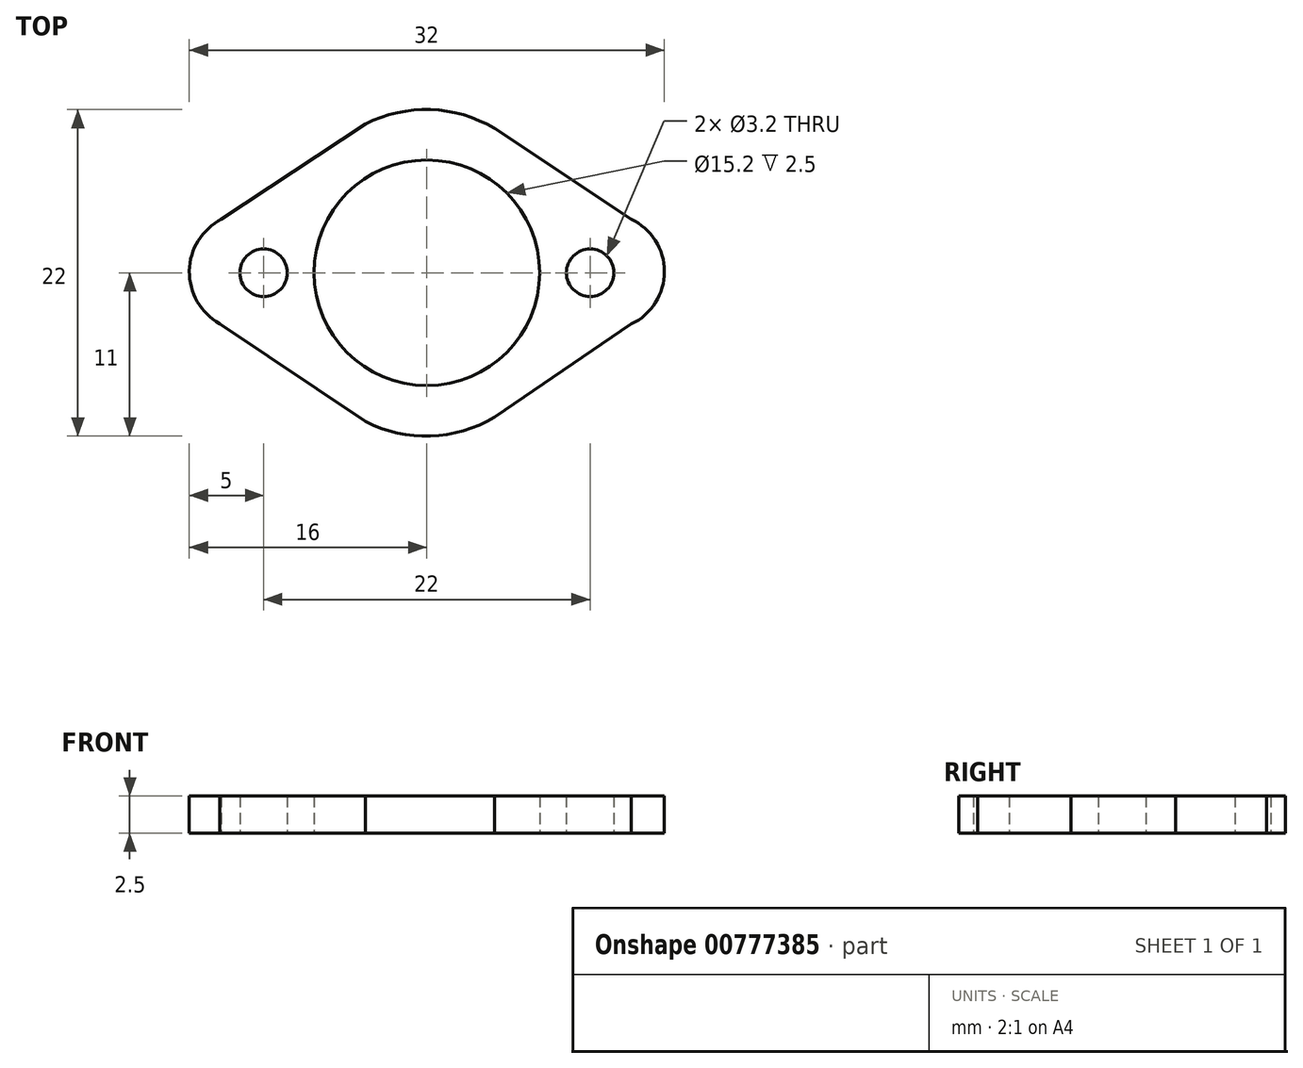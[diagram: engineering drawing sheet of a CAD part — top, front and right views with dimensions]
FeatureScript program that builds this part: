
annotation { "Feature Type Name" : "Feature", "Feature Type Description" : "" }
export const myFeature = defineFeature(function(context is Context, id is Id, definition is map)
    precondition{}
    {
        {
            var Q0;
            Q0=qCreatedBy(makeId("Top.planeOp"),FACE);
            var sketch = newSketch(context, id + "F0", { "sketchPlane" : qUnion([Q0])});
            skCircle(sketch, "E0", {"center": v(0, 0) * mm, "radius": 7.6 * mm});
            skCircle(sketch, "E1", {"center": v(11, 0) * mm, "radius": 1.6 * mm});
            skCircle(sketch, "E2", {"center": v(-11, 0) * mm, "radius": 1.6 * mm});
            skLineSegment(sketch, "E3", {"start": v(-13.34, 2.74) * mm, "end": v(-3.64, 9.15) * mm});
            skLineSegment(sketch, "E4", {"start": v(4.01, 8.89) * mm, "end": v(13.28, 2.74) * mm});
            skLineSegment(sketch, "E5", {"start": v(13.28, -2.58) * mm, "end": v(4.02, -8.88) * mm});
            skLineSegment(sketch, "E6", {"start": v(-3.64, -9.16) * mm, "end": v(-13.43, -2.58) * mm});
            skPoint(sketch, "E7.visualSharp", {"position": v(-21.18, 0) * mm});
            skArc(sketch, "E7.filletArc", {"start": v(-13.34, 2.74) * mm, "mid": v(-15, 0.1) * mm, "end": v(-13.43, -2.58) * mm});
            skPoint(sketch, "E8.visualSharp", {"position": v(0, 10.6) * mm});
            skArc(sketch, "E8.filletArc", {"start": v(4.01, 8.89) * mm, "mid": v(0.22, 10) * mm, "end": v(-3.64, 9.15) * mm});
            skPoint(sketch, "E9.visualSharp", {"position": v(17.4, 0) * mm});
            skArc(sketch, "E9.filletArc", {"start": v(13.28, -2.58) * mm, "mid": v(15, 0.08) * mm, "end": v(13.28, 2.74) * mm});
            skPoint(sketch, "E10.visualSharp", {"position": v(0, -10.6) * mm});
            skArc(sketch, "E10.filletArc", {"start": v(-3.64, -9.16) * mm, "mid": v(0.23, -10) * mm, "end": v(4.02, -8.88) * mm});
            skLineSegment(sketch, "E11.0", {"start": v(4.54, 9.73) * mm, "end": v(13.77, 3.61) * mm});
            skArc(sketch, "E11.1", {"start": v(13.77, -3.45) * mm, "mid": v(16, 0.08) * mm, "end": v(13.77, 3.61) * mm});
            skArc(sketch, "E11.2", {"start": v(4.54, 9.73) * mm, "mid": v(0.24, 11) * mm, "end": v(-4.14, 10.02) * mm});
            skLineSegment(sketch, "E11.3", {"start": v(13.77, -3.45) * mm, "end": v(4.56, -9.73) * mm});
            skLineSegment(sketch, "E11.4", {"start": v(-13.84, 3.6) * mm, "end": v(-4.14, 10.02) * mm});
            skArc(sketch, "E11.5", {"start": v(-13.84, 3.6) * mm, "mid": v(-16, 0.12) * mm, "end": v(-13.95, -3.44) * mm});
            skLineSegment(sketch, "E11.6", {"start": v(-4.14, -10.02) * mm, "end": v(-13.95, -3.44) * mm});
            skArc(sketch, "E11.7", {"start": v(-4.14, -10.02) * mm, "mid": v(0.25, -11) * mm, "end": v(4.56, -9.73) * mm});
            skSolve(sketch);
        }
        {
            var Q0;
            Q0=makeQuery(id+"F0.imprint","IMPRINT",FACE,{"disambiguationData":[TD([[makeQuery(id+"F0.imprint","IMPRINT",EDGE,{"derivedFrom":sQuery(id+"F0.wireOp",EDGE,"E3")}),1.0]])]});
            var Q1;
            Q1=makeQuery(id+"F0.imprint","IMPRINT",FACE,{"disambiguationData":[TD([[makeQuery(id+"F0.imprint","IMPRINT",EDGE,{"derivedFrom":sQuery(id+"F0.wireOp",EDGE,"E0")}),-1.0]])]});
            extrude(context, id + "F1", {"entities" : qUnion([Q0, Q1]), "depth" : 2.5 * mm, "offsetDistance" : 25 * mm});
        }
    });
